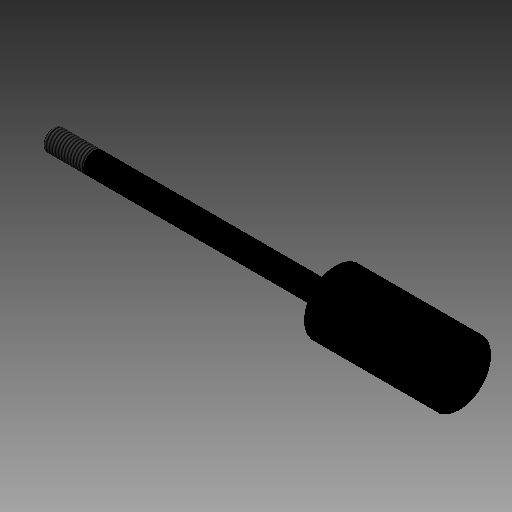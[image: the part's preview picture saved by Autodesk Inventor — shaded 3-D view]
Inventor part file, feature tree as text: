
AUTODESK INVENTOR PART (.ipt)
format: ipt  version: 2018.3 (Build 223284000, 284)  size: 147,968 bytes
history: native  units: in
note: dims shown in document units (in); Inventor stores cm internally (conversion verified against a paired STEP export)
features: other x70, revolve x3, sketch x3, thread x1
ambient origin geometry x8: Origin, YZ Plane, XZ Plane, XY Plane, X Axis, Y Axis, Z Axis, Center Point
bodies: Solid1 (feature_tree)
feature tree (77):
  revolve  "Revolution1"  Angle=360.0deg
  revolve  "Revolution2"  Angle=360.0deg
  thread  "Thread1"  [1 undecoded]
  revolve  "Revolution3"  [1 undecoded]
  other  "dia1_XY"
  other  "dia1_YZ"
  other  "dia1_ZX"
  other  "dia1_X"
  other  "dia1_Y"
  other  "dia1_Z"
  other  "dia1_Center"
  other  "dia12_XY"
  other  "dia12_YZ"
  other  "dia12_ZX"
  other  "dia12_X"
  other  "dia12_Y"
  other  "dia12_Z"
  other  "dia12_Center"
  other  "dia2_XY"
  other  "dia2_YZ"
  other  "dia2_ZX"
  other  "dia2_X"
  other  "dia2_Y"
  other  "dia2_Z"
  other  "dia2_Center"
  other  "dia22_XY"
  other  "dia22_YZ"
  other  "dia22_ZX"
  other  "dia22_X"
  other  "dia22_Y"
  other  "dia22_Z"
  other  "dia22_Center"
  other  "rl1_XY"
  other  "rl1_YZ"
  other  "rl1_ZX"
  other  "rl1_X"
  other  "rl1_Y"
  other  "rl1_Z"
  other  "rl1_Center"
  other  "rl2_XY"
  other  "rl2_YZ"
  other  "rl2_ZX"
  other  "rl2_X"
  other  "rl2_Y"
  other  "rl2_Z"
  other  "rl2_Center"
  other  "rod_cp_XY"
  other  "rod_cp_YZ"
  other  "rod_cp_ZX"
  other  "rod_cp_X"
  other  "rod_cp_Y"
  other  "rod_cp_Z"
  other  "rod_cp_Center"
  other  "thd1_XY"
  other  "thd1_YZ"
  other  "thd1_ZX"
  other  "thd1_X"
  other  "thd1_Y"
  other  "thd1_Z"
  other  "thd1_Center"
  other  "thd2_XY"
  other  "thd2_YZ"
  other  "thd2_ZX"
  other  "thd2_X"
  other  "thd2_Y"
  other  "thd2_Z"
  other  "thd2_Center"
  other  "to_rod_clevis_XY"
  other  "to_rod_clevis_YZ"
  other  "to_rod_clevis_ZX"
  other  "to_rod_clevis_X"
  other  "to_rod_clevis_Y"
  other  "to_rod_clevis_Z"
  other  "to_rod_clevis_Center"
  sketch  "Sketch_1"  dims[d0=360.0deg d1=360.0deg]
  sketch  "Sketch_3"  dims[d2=0.4787in d3=0.0in d4=360.0deg]
  sketch  "Sketch_30"  dims[d5=0.0in d6=0.0in d7=0.0in d8=0.0in d9=0.0in]
note: 2 required parameter values undecoded (feature->parameter linkage not recoverable at this tier; creation-order binding heuristic only, values carry confidence <= 0.55)
